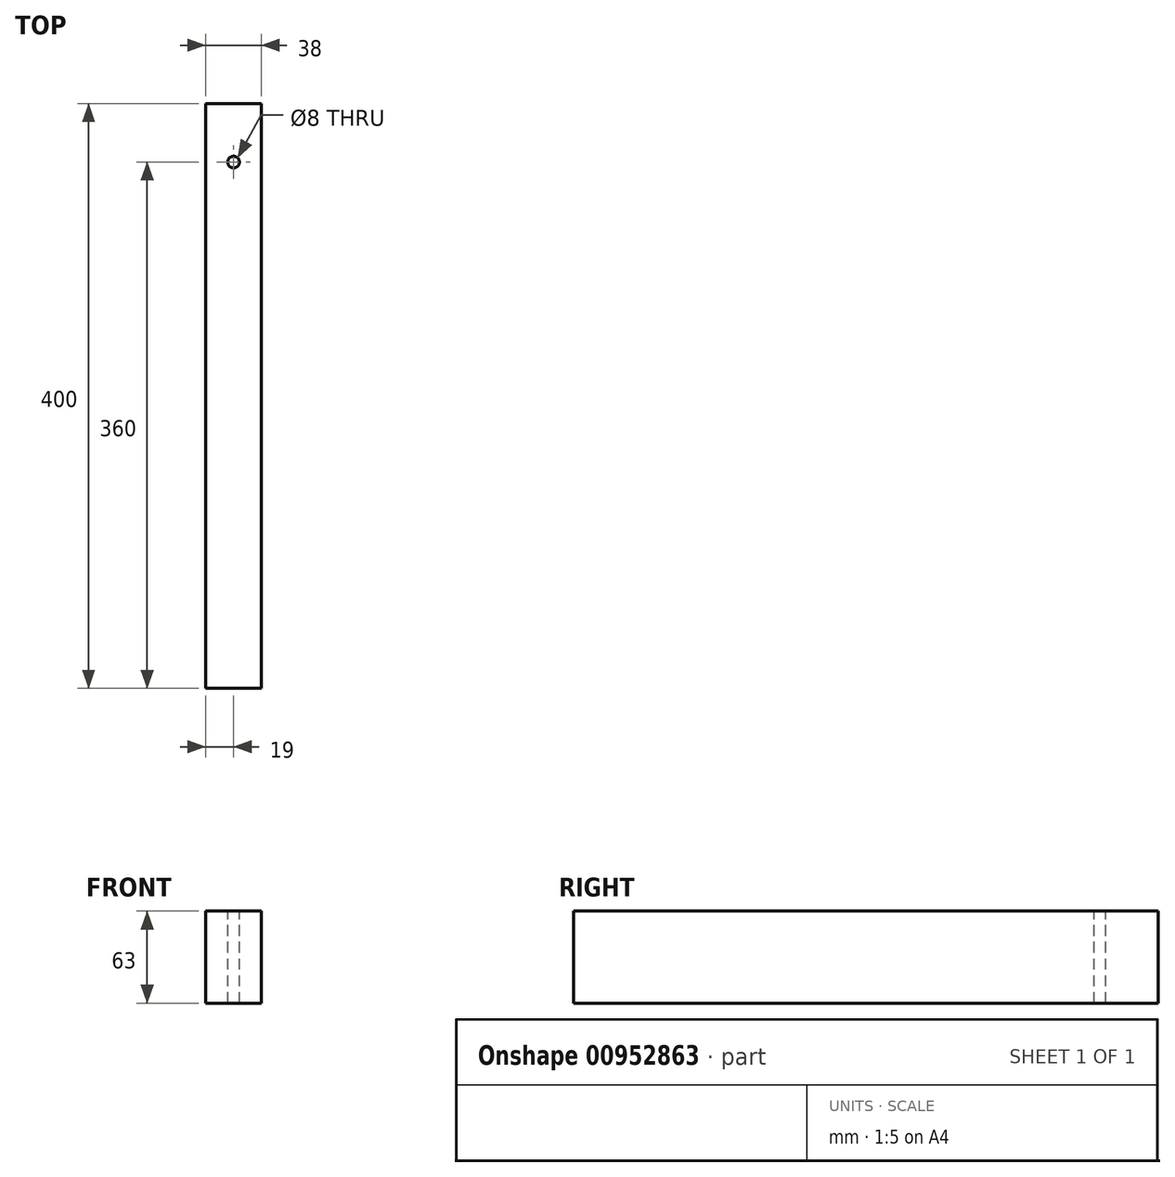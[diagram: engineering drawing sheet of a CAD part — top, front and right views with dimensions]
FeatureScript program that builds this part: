
annotation { "Feature Type Name" : "Feature", "Feature Type Description" : "" }
export const myFeature = defineFeature(function(context is Context, id is Id, definition is map)
    precondition{}
    {
        {
            var Q0;
            Q0=qCreatedBy(makeId("Front.planeOp"),FACE);
            var sketch = newSketch(context, id + "F0", { "sketchPlane" : qUnion([Q0])});
            skLineSegment(sketch, "E0.bottom", {"start": v(0, 0) * mm, "end": v(38, 0) * mm});
            skLineSegment(sketch, "E0.top", {"start": v(0, 63) * mm, "end": v(38, 63) * mm});
            skLineSegment(sketch, "E0.left", {"start": v(0, 0) * mm, "end": v(0, 63) * mm});
            skLineSegment(sketch, "E0.right", {"start": v(38, 0) * mm, "end": v(38, 63) * mm});
            skSolve(sketch);
        }
        {
            var Q0;
            Q0 = qSketchRegion(id + "F0", true);
            extrude(context, id + "F1", {"entities" : qUnion([Q0]), "depth" : 400 * mm, "offsetDistance" : 25 * mm});
        }
        {
            var Q0;
            Q0=makeQuery(id+"F1.opExtrude","SWEPT_FACE",FACE,{"disambiguationData":[OSD([sQuery(id+"F0.wireOp",EDGE,"E0.top")])]});
            var sketch = newSketch(context, id + "F2", { "sketchPlane" : qUnion([Q0])});
            skLineSegment(sketch, "E1", {"start": v(19, 0) * mm, "end": v(19, -40) * mm, "construction": true});
            skCircle(sketch, "E2", {"center": v(19, -40) * mm, "radius": 4 * mm});
            skSolve(sketch);
        }
        {
            var Q0;
            Q0 = qSketchRegion(id + "F2", true);
            extrude(context, id + "F3", {"entities" : qUnion([Q0]), "operationType" : NewBodyOperationType.REMOVE, "endBound" : BoundingType.UP_TO_NEXT, "oppositeDirection" : true, "depth" : 25 * mm, "offsetDistance" : 25 * mm});
        }
    });
